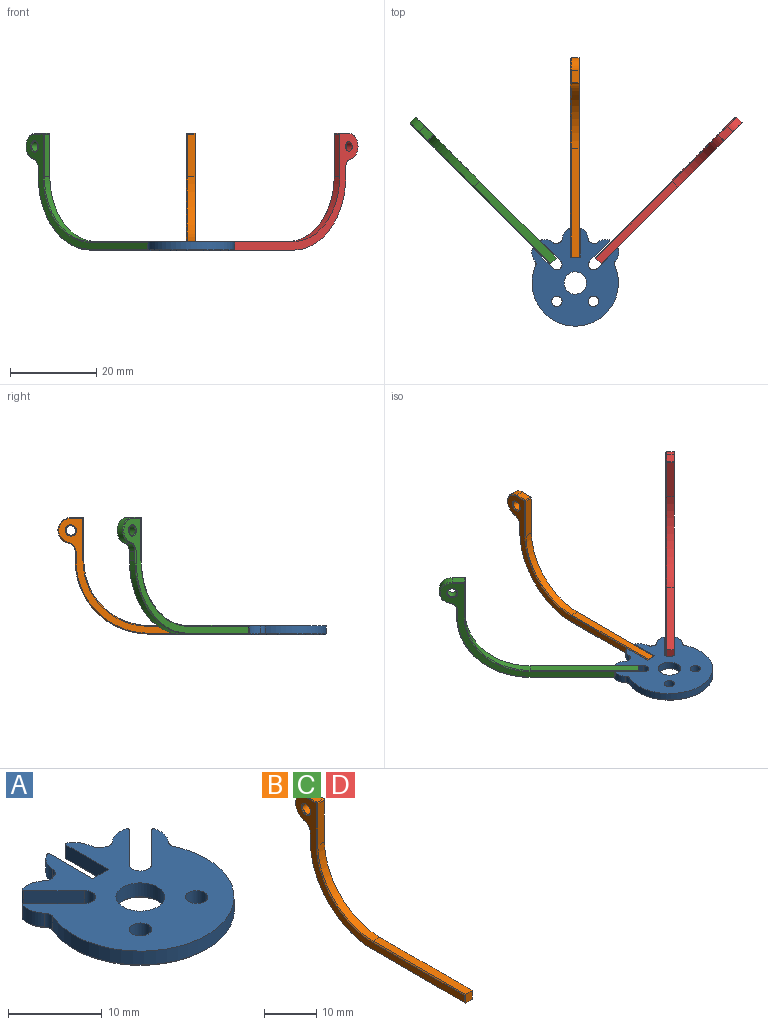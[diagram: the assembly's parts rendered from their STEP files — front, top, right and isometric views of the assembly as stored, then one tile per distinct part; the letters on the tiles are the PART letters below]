
ASSEMBLY  parts=4 mates=3
PART A: 68 faces, bbox 20.1x22.6x2 mm
  f0: cylinder r=2.6mm len=5.2mm, axis (0,0,1), area 29.4mm2, adj f4,f65
  f1: cylinder r=1.2mm len=2.4mm, axis (0,0,1), area 13.6mm2, adj f4,f66
  f2: cylinder r=1.2mm len=2.4mm, axis (0,0,1), area 13.6mm2, adj f4,f67
  f3: plane 22.23x19.74mm, normal (0,0,-1), area 245.3mm2, adj f36,f37,f38,f39,f40,f41,f42,f44
  f4: plane 22.63x20.14mm, normal (0,0,1), area 275mm2, adj f0,f1,f2,f5,f6,f7,f8,f9
  f5: cylinder r=3mm len=2.76mm, axis (0,0,1), area 5.3mm2, adj f4,f28,f34,f56
  f6: cylinder r=10mm len=20mm, axis (0,0,1), area 71.5mm2, adj f4,f27,f28,f60
  f7: cylinder r=3mm len=2.76mm, axis (0,0,1), area 5.3mm2, adj f4,f27,f33,f64
  f8: plane 4.54x4.54mm, normal (-0.71,0.71,0), area 11.6mm2, adj f4,f9,f33,f61
  f9: cylinder r=1.2mm len=2.05mm, axis (0,0,1), area 6.8mm2, adj f4,f8,f10,f59
  f10: plane 4.54x4.54mm, normal (0.71,-0.71,0), area 11.6mm2, adj f4,f9,f32,f57
  f11: cylinder r=3mm len=2.76mm, axis (0,0,1), area 5.3mm2, adj f4,f26,f32,f53
  f12: cylinder r=10mm len=1.8mm, axis (0,0,1), area 0.8mm2, adj f4,f25,f26,f49
  f13: cylinder r=3mm len=2.41mm, axis (0,0,1), area 5.3mm2, adj f4,f25,f31,f45
  f14: plane 6.43x1.8mm, normal (-1,0,0), area 11.6mm2, adj f4,f15,f31,f41
  f15: plane 2.4x1.8mm, normal (0,1,0), area 4.3mm2, adj f4,f14,f16,f39
  f16: plane 6.43x1.8mm, normal (1,0,0), area 11.6mm2, adj f4,f15,f30,f37
  f17: cylinder r=3mm len=2.41mm, axis (0,0,1), area 5.3mm2, adj f4,f24,f30,f36
  f18: cylinder r=10mm len=1.8mm, axis (0,0,1), area 0.8mm2, adj f4,f23,f24,f40
  f19: cylinder r=3mm len=2.76mm, axis (0,0,1), area 5.3mm2, adj f4,f23,f29,f44
  f20: plane 4.54x4.54mm, normal (-0.71,-0.71,0), area 11.6mm2, adj f4,f21,f29,f48
  f21: cylinder r=1.2mm len=2.05mm, axis (0,0,1), area 6.8mm2, adj f4,f20,f22,f50
  f22: plane 4.54x4.54mm, normal (0.71,0.71,0), area 11.6mm2, adj f4,f21,f34,f52
  f23: cylinder r=1mm len=1.8mm, axis (0,0,-1), area 2mm2, adj f4,f18,f19,f42
  f24: cylinder r=1mm len=1.8mm, axis (0,0,-1), area 2mm2, adj f4,f17,f18,f38
  f25: cylinder r=1mm len=1.8mm, axis (0,0,-1), area 2mm2, adj f4,f12,f13,f47
  f26: cylinder r=1mm len=1.8mm, axis (0,0,-1), area 2mm2, adj f4,f11,f12,f51
  f27: cylinder r=1mm len=1.8mm, axis (0,0,-1), area 2mm2, adj f4,f6,f7,f62
  f28: cylinder r=1mm len=1.8mm, axis (0,0,-1), area 2mm2, adj f4,f5,f6,f58
  f29: cylinder r=0.2mm len=1.8mm, axis (0,0,1), area 0.8mm2, adj f4,f19,f20,f46
  f30: cylinder r=0.2mm len=1.8mm, axis (0,0,1), area 0.8mm2, adj f4,f16,f17,f35
  f31: cylinder r=0.2mm len=1.8mm, axis (0,0,1), area 0.8mm2, adj f4,f13,f14,f43
  f32: cylinder r=0.2mm len=1.8mm, axis (0,0,1), area 0.8mm2, adj f4,f10,f11,f55
  f33: cylinder r=0.2mm len=1.8mm, axis (0,0,1), area 0.8mm2, adj f4,f7,f8,f63
  f34: cylinder r=0.2mm len=1.8mm, axis (0,0,1), area 0.8mm2, adj f4,f5,f22,f54
  f35: cone r=0.2mm half-angle=45deg, axis (0,0,1), area 0.1mm2, adj f30,f36,f37
  f36: cone r=3mm half-angle=45deg, axis (0,0,1), area 0.8mm2, adj f3,f17,f35,f38
  f37: plane 6.63x0.2mm, normal (0.71,0,-0.71), area 1.8mm2, adj f3,f16,f35,f39
  f38: cone r=1.2mm half-angle=45deg, axis (0,0,-1), area 0.4mm2, adj f3,f24,f36,f40
  f39: plane 2.8x0.2mm, normal (0,0.71,-0.71), area 0.7mm2, adj f3,f15,f37,f41
  f40: cone r=10mm half-angle=45deg, axis (0,0,1), area 0.1mm2, adj f3,f18,f38,f42
  f41: plane 6.63x0.2mm, normal (-0.71,0,-0.71), area 1.8mm2, adj f3,f14,f39,f43
  f42: cone r=1.2mm half-angle=45deg, axis (0,0,-1), area 0.4mm2, adj f3,f23,f40,f44
  f43: cone r=0.2mm half-angle=45deg, axis (0,0,1), area 0.1mm2, adj f31,f41,f45
  f44: cone r=3mm half-angle=45deg, axis (0,0,1), area 0.8mm2, adj f3,f19,f42,f46
  f45: cone r=3mm half-angle=45deg, axis (0,0,1), area 0.8mm2, adj f3,f13,f43,f47
  f46: cone r=0.2mm half-angle=45deg, axis (0,0,1), area 0.1mm2, adj f29,f44,f48
  f47: cone r=1.2mm half-angle=45deg, axis (0,0,-1), area 0.4mm2, adj f3,f25,f45,f49
  f48: plane 4.68x4.68mm, normal (-0.5,-0.5,-0.71), area 1.8mm2, adj f3,f20,f46,f50
  f49: cone r=10mm half-angle=45deg, axis (0,0,1), area 0.1mm2, adj f3,f12,f47,f51
  f50: cone r=1.2mm half-angle=45deg, axis (0,0,-1), area 1.2mm2, adj f3,f21,f48,f52
  f51: cone r=1.2mm half-angle=45deg, axis (0,0,-1), area 0.4mm2, adj f3,f26,f49,f53
  f52: plane 4.68x4.68mm, normal (0.5,0.5,-0.71), area 1.8mm2, adj f3,f22,f50,f54
  f53: cone r=3mm half-angle=45deg, axis (0,0,1), area 0.8mm2, adj f3,f11,f51,f55
  f54: cone r=0.2mm half-angle=45deg, axis (0,0,1), area 0.1mm2, adj f34,f52,f56
  f55: cone r=0.2mm half-angle=45deg, axis (0,0,1), area 0.1mm2, adj f32,f53,f57
  f56: cone r=3mm half-angle=45deg, axis (0,0,1), area 0.8mm2, adj f3,f5,f54,f58
  f57: plane 4.68x4.68mm, normal (0.5,-0.5,-0.71), area 1.8mm2, adj f3,f10,f55,f59
  f58: cone r=1.2mm half-angle=45deg, axis (0,0,-1), area 0.4mm2, adj f3,f28,f56,f60
  f59: cone r=1.2mm half-angle=45deg, axis (0,0,-1), area 1.2mm2, adj f3,f9,f57,f61
  f60: cone r=10mm half-angle=45deg, axis (0,0,1), area 11.1mm2, adj f3,f6,f58,f62
  f61: plane 4.68x4.68mm, normal (-0.5,0.5,-0.71), area 1.8mm2, adj f3,f8,f59,f63
  f62: cone r=1.2mm half-angle=45deg, axis (0,0,-1), area 0.4mm2, adj f3,f27,f60,f64
  f63: cone r=0.2mm half-angle=45deg, axis (0,0,1), area 0.1mm2, adj f33,f61,f64
  f64: cone r=3mm half-angle=45deg, axis (0,0,1), area 0.8mm2, adj f3,f7,f62,f63
  f65: cone r=2.8mm half-angle=45deg, axis (0,0,-1), area 4.8mm2, adj f0,f3
  f66: cone r=1.4mm half-angle=45deg, axis (0,0,-1), area 2.3mm2, adj f1,f3
  f67: cone r=1.4mm half-angle=45deg, axis (0,0,-1), area 2.3mm2, adj f2,f3
PART B: 26 faces, bbox 2x46.1x27 mm
  f0: plane 2x1.8mm, normal (0,-1,0), area 3.6mm2, adj f1,f9,f10,f18
  f1: plane 25.1x1.8mm, normal (0,0,-1), area 45.2mm2, adj f0,f2,f10,f16
  f2: cylinder r=17mm len=17mm, axis (-1,0,0), area 48.1mm2, adj f1,f3,f10,f14
  f3: plane 2.1x1.8mm, normal (0,1,0), area 3.8mm2, adj f2,f10,f12,f15
  f4: cylinder r=3mm len=5.94mm, axis (-1,0,0), area 15.9mm2, adj f5,f10,f12,f19
  f5: plane 2.8x1.8mm, normal (0,0,1), area 5mm2, adj f4,f10,f13,f21
  f6: plane 9.8x1.8mm, normal (0,-1,0), area 17.6mm2, adj f7,f10,f13,f24
  f7: cylinder r=15mm len=15mm, axis (-1,0,0), area 42.4mm2, adj f6,f9,f10,f22
  f8: cylinder r=1.1mm len=2.2mm, axis (-1,0,0), area 12.4mm2, adj f10,f25
  f9: plane 25.1x1.8mm, normal (0,0,1), area 45.2mm2, adj f0,f7,f10,f20
  f10: plane 46.1x27mm, normal (1,0,0), area 137.5mm2, adj f0,f1,f2,f3,f4,f5,f6,f7
  f11: plane 45.7x26.6mm, normal (-1,0,0), area 110.3mm2, adj f14,f15,f16,f17,f18,f19,f20,f21
  f12: cylinder r=2mm len=1.96mm, axis (-1,0,0), area 4.9mm2, adj f3,f4,f10,f17
  f13: cylinder r=0.2mm len=1.8mm, axis (-1,0,0), area 0.6mm2, adj f5,f6,f10,f23
  f14: cone r=17mm half-angle=45deg, axis (1,0,0), area 7.5mm2, adj f2,f11,f15,f16
  f15: plane 2.1x0.2mm, normal (-0.71,0.71,0), area 0.6mm2, adj f3,f11,f14,f17
  f16: plane 25.1x0.2mm, normal (-0.71,0,-0.71), area 7.1mm2, adj f1,f11,f14,f18
  f17: cone r=2.2mm half-angle=45deg, axis (-1,0,0), area 0.8mm2, adj f11,f12,f15,f19
  f18: plane 2x0.2mm, normal (-0.71,-0.71,0), area 0.5mm2, adj f0,f11,f16,f20
  f19: cone r=2.8mm half-angle=45deg, axis (1,0,0), area 2.4mm2, adj f4,f11,f17,f21
  f20: plane 25.1x0.2mm, normal (-0.71,0,0.71), area 7.1mm2, adj f9,f11,f18,f22
  f21: plane 2.8x0.2mm, normal (-0.71,0,0.71), area 0.8mm2, adj f5,f11,f19,f23
  f22: cone r=15.2mm half-angle=45deg, axis (-1,0,0), area 6.7mm2, adj f7,f11,f20,f24
  f23: cone r=0.2mm half-angle=45deg, axis (1,0,0), area 0mm2, adj f13,f21,f24
  f24: plane 9.8x0.2mm, normal (-0.71,-0.71,0), area 2.8mm2, adj f6,f11,f22,f23
  f25: cone r=1.3mm half-angle=45deg, axis (-1,0,0), area 2.1mm2, adj f8,f11
PART C: same geometry as B
PART D: same geometry as B
PLACE A at identity fixed
PLACE B t=(-0.1,0,0.1)mm
PLACE C rot(axis=(0,0,1),45deg) t=(-0.85,0.83,0.1)mm
PLACE D rot(axis=(0,0,-1),45deg) t=(1.07,0.91,0.1)mm
MATE planar B.f1 <-> D.f1  axis (0,0,-1) through (0,18.55,0.1)mm
MATE planar B.f1 <-> C.f1  axis (0,0,-1) through (0,18.55,0.1)mm
MATE fastened A.f15 <-> B.f0  axis (0,1,0) through (0,6,1.1)mm
